# Revit family: CADS_AIRFLOWdev_AirflexPro_Round_90DegFloorOutlet_Extract
name_source: partatom
category: Duct Fittings
revit_build: Autodesk Revit 2015 (Build: 20160512_1515(x64)
units: mm (PartAtom-declared; Revit-internal decimal feet)

## types (1)
- CADS_AIRFLOWdev_AirflexPro_Round_90DegFloorOutlet_Extract
    6MonthlyMaintenance = Visually inspect system, clean the fan and ducting if necessary
    AF_Body = AF_Grey
    AirflowRateRange = 18.0 L/s
    AssemblyPlace = UNKNOWN
    AssetType = FIXED
    CADS_Index = 0
    CEApproval = Yes
    Color = Silver
    Constituents = Round 90o floor plenum for use with 9041174
    DurationUnit = Year
    ExpectedServiceLife = 10
    Features = Round 90o floor plenum for use with 9041174
    Finish = Lacquer
    FireControlPanelLinks = No
    Fitting Type = Ignore
    Grade = Stainless
    GrossWeight = 1.10 kg
    ISO140001 = Yes
    ISO90001 = Yes
    IsExtendedWarranty = No
    LongitudinalSeam = None
    Manufacturer = Airflow Developments Ltd
    ManufacturerAddress = Aidelle House
Lancaster Road
Cressex Business Park
High Wycombe
Bucks
HP123QP
    ManufacturerTelephone = 01494 525252
    ManufacturerWebsite = www.airflow.com
    Material = Steel
    NBSCode = 45-80-50/394 Ventilation ducts
    NominalHeight = 385 mm
    NominalLength = 245 mm
    NominalWidth = 190 mm
    PassiveHouseApproval = No
    PointOfContact = Airflow Developments Ltd
    ProductLiterature = https://www.airflow.com
    ProductionYear = 2017
    Quantity = 1
    RedDotDesignAward = No
    ReplacementCost = 71.208
    RunID = 0
    SAPApproval = Yes
    ServiceLifeDuration = 10
    ServiceLifeType = EXPECTEDSERVICELIFE
    Shape = Other
    ShippingWeight = 1.32 kg
    Size = 245x 190x  385
    Status = New
    TemperatureRange = up to 40°C
    Uniclass2015 = Pr_30_59_96_92:Ventilation ducts
    WarrantyGuarantor = Airflow Developments Ltd
    WarrantyPeriod = 0
    WorkingPressure = 3000.0 Pa

## geometry (parser evidence)
native form markers: Blend x4, Sweep x1
no freeform markers — native parametric forms only
